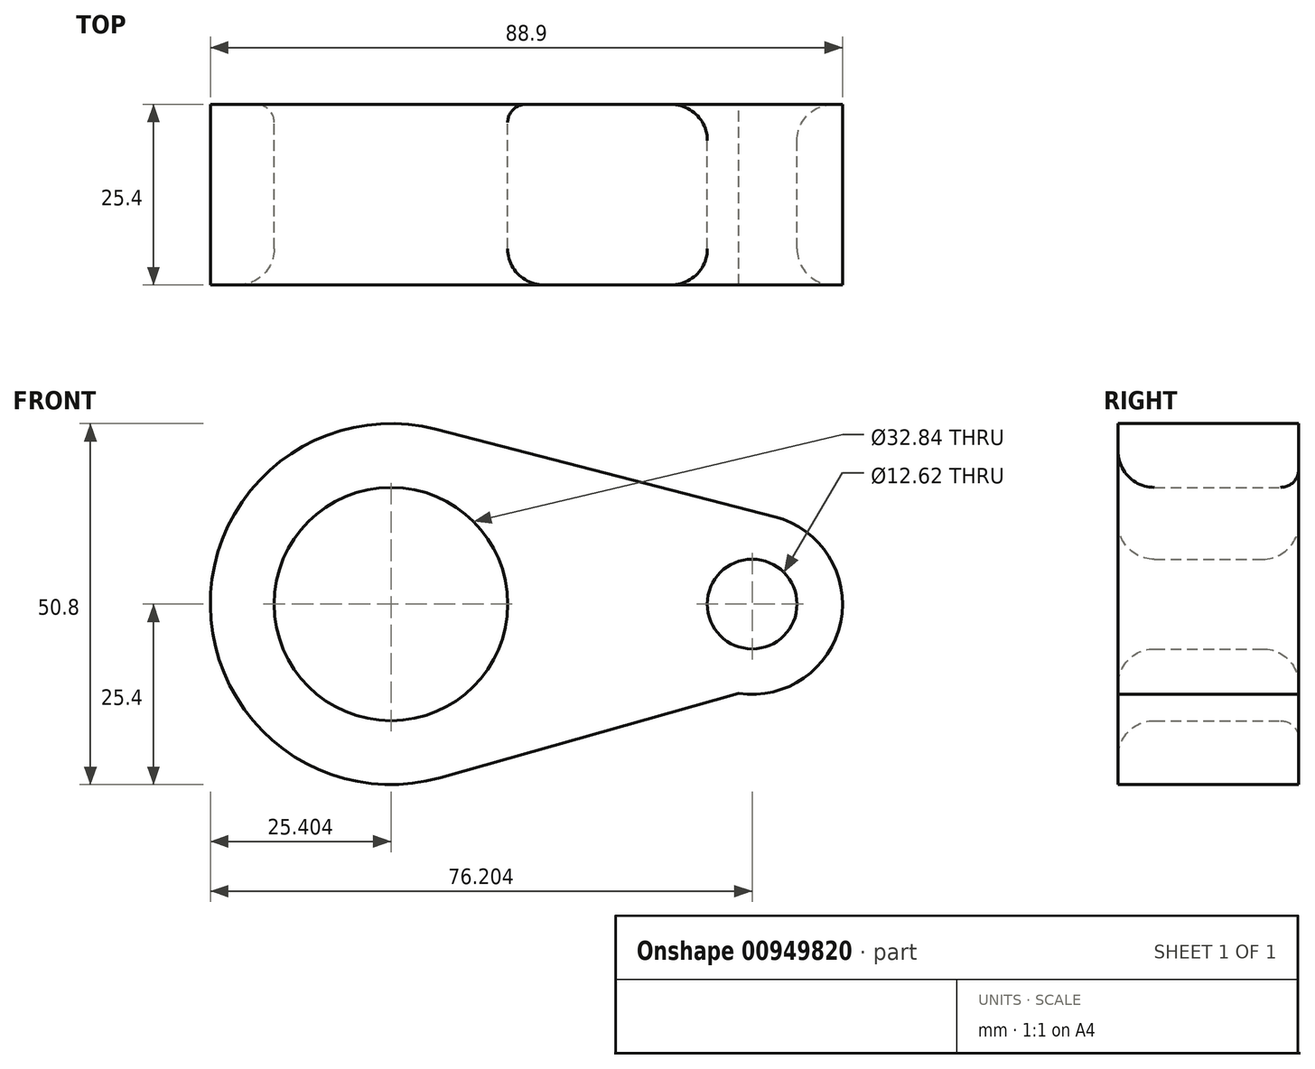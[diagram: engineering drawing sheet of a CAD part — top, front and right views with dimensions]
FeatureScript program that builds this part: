
annotation { "Feature Type Name" : "Feature", "Feature Type Description" : "" }
export const myFeature = defineFeature(function(context is Context, id is Id, definition is map)
    precondition{}
    {
        {
            var Q0;
            Q0=qCreatedBy(makeId("Front.planeOp"),FACE);
            var sketch = newSketch(context, id + "F0", { "sketchPlane" : qUnion([Q0])});
            skCircle(sketch, "E0", {"center": v(-64.23, 0) * mm, "radius": 25.4 * mm});
            skCircle(sketch, "E1", {"center": v(-13.43, 0) * mm, "radius": 12.7 * mm});
            skLineSegment(sketch, "E2", {"start": v(-57.88, 24.6) * mm, "end": v(-10.25, 12.3) * mm});
            skLineSegment(sketch, "E3", {"start": v(-15.34, -12.56) * mm, "end": v(-57.3, -24.44) * mm});
            skCircle(sketch, "E4", {"center": v(-64.23, 0) * mm, "radius": 16.42 * mm});
            skCircle(sketch, "E5", {"center": v(-13.43, 0) * mm, "radius": 6.31 * mm});
            skSolve(sketch);
        }
        {
            var Q0;
            Q0=makeQuery(id+"F0.imprint","IMPRINT",FACE,{"disambiguationData":[TD([[makeQuery(id+"F0.imprint","IMPRINT",EDGE,{"derivedFrom":sQuery(id+"F0.wireOp",EDGE,"E4")}),-1.0]])]});
            var Q1;
            {var subQ0=sQuery(id+"F0.wireOp",EDGE,"E2");Q1=makeQuery(id+"F0.imprint","IMPRINT",FACE,{"disambiguationData":[TD([[makeQuery(id+"F0.imprint","IMPRINT",EDGE,{"derivedFrom":subQ0}),-1.0]])]});}
            var Q2;
            Q2=makeQuery(id+"F0.imprint","IMPRINT",FACE,{"disambiguationData":[TD([[makeQuery(id+"F0.imprint","IMPRINT",EDGE,{"derivedFrom":sQuery(id+"F0.wireOp",EDGE,"E5")}),-1.0]])]});
            extrude(context, id + "F1", {"entities" : qUnion([Q0, Q1, Q2]), "depth" : 25.4 * mm, "offsetDistance" : 25.4 * mm});
        }
        {
            var Q0;
            Q0=makeQuery(id+"F1.opExtrude","CAP_EDGE",EDGE,{"disambiguationData":[OSD([sQuery(id+"F0.wireOp",EDGE,"E4")])],"isStart":false});
            var Q1;
            Q1=makeQuery(id+"F1.opExtrude","SWEPT_FACE",FACE,{"disambiguationData":[OSD([sQuery(id+"F0.wireOp",EDGE,"E5")])]});
            fillet(context, id + "F2", {"entities" : qUnion([Q0, Q1]), "radius" : 5.08 * mm, "tangentPropagation" : true, "allowEdgeOverflow" : false});
        }
        {
            var Q0;
            Q0=makeQuery(id+"F1.opExtrude","CAP_EDGE",EDGE,{"disambiguationData":[OSD([sQuery(id+"F0.wireOp",EDGE,"E4")])],"isStart":true});
            fillet(context, id + "F3", {"entities" : qUnion([Q0]), "tangentPropagation" : true, "radius" : 2.54 * mm, "defaultsChanged" : true, "vertexSettings" : [], "allowEdgeOverflow" : false});
        }
    });
